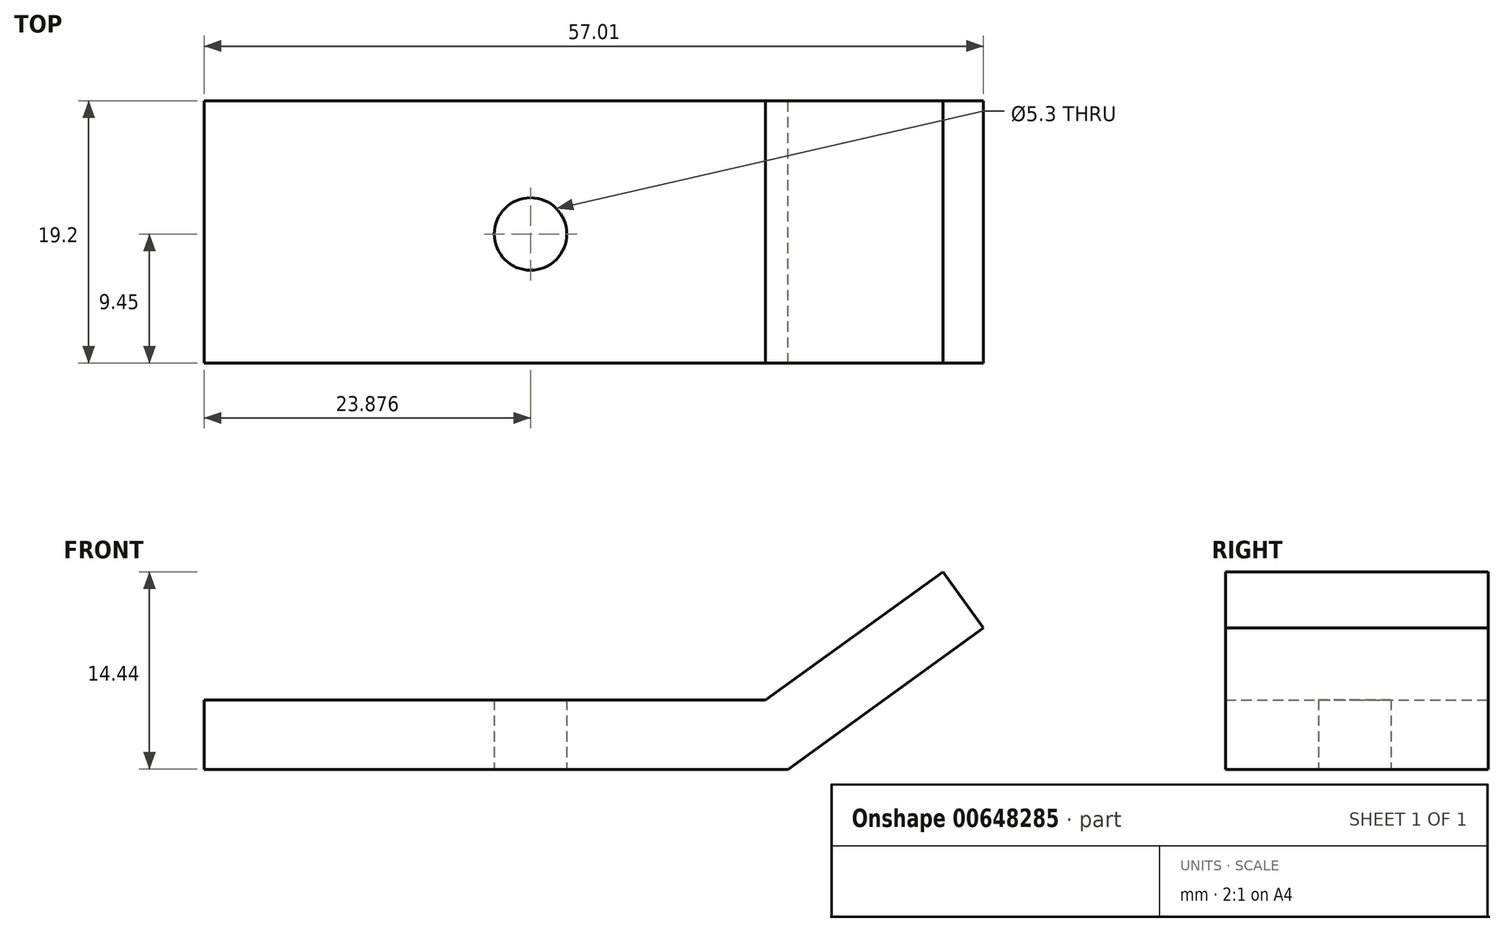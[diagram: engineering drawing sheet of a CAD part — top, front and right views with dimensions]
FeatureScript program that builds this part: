
annotation { "Feature Type Name" : "Feature", "Feature Type Description" : "" }
export const myFeature = defineFeature(function(context is Context, id is Id, definition is map)
    precondition{}
    {
        {
            var Q0;
            Q0=qCreatedBy(makeId("Front.planeOp"),FACE);
            var sketch = newSketch(context, id + "F0", { "sketchPlane" : qUnion([Q0])});
            skLineSegment(sketch, "E0", {"start": v(-38.7, -7.25) * mm, "end": v(4, -7.25) * mm});
            skLineSegment(sketch, "E1", {"start": v(4, -7.25) * mm, "end": v(18.3, 3.07) * mm});
            skLineSegment(sketch, "E2.0", {"start": v(2.36, -2.17) * mm, "end": v(15.33, 7.19) * mm});
            skLineSegment(sketch, "E3", {"start": v(2.36, -2.17) * mm, "end": v(-38.7, -2.17) * mm});
            skLineSegment(sketch, "E4", {"start": v(-38.7, -7.25) * mm, "end": v(-38.7, -2.17) * mm});
            skLineSegment(sketch, "E5", {"start": v(15.33, 7.19) * mm, "end": v(18.3, 3.07) * mm});
            skSolve(sketch);
        }
        {
            var Q0;
            Q0=makeQuery(id+"F0.imprint","IMPRINT",FACE,{"disambiguationData":[TD([[makeQuery(id+"F0.imprint","IMPRINT",EDGE,{"derivedFrom":sQuery(id+"F0.wireOp",EDGE,"E0")}),1.0]])]});
            var sketch = newSketch(context, id + "F1", { "sketchPlane" : qUnion([Q0])});
            skSolve(sketch);
        }
        {
            var Q0;
            Q0=makeQuery(id+"F0.imprint","IMPRINT",FACE,{"disambiguationData":[TD([[makeQuery(id+"F0.imprint","IMPRINT",EDGE,{"derivedFrom":sQuery(id+"F0.wireOp",EDGE,"E0")}),1.0]])]});
            extrude(context, id + "F2", {"entities" : qUnion([Q0]), "endBound" : BoundingType.SYMMETRIC, "depth" : 19.2 * mm, "offsetDistance" : 25.4 * mm});
        }
        {
            var Q0;
            Q0=makeQuery(id+"F1.imprint","IMPRINT",FACE,{"disambiguationData":[TD([[makeQuery(id+"F1.imprint","IMPRINT",EDGE,{"derivedFrom":makeQuery(id+"F0.imprint","IMPRINT",EDGE,{"derivedFrom":sQuery(id+"F0.wireOp",EDGE,"E0")})}),1.0]])]});
            var sketch = newSketch(context, id + "F3", { "sketchPlane" : qUnion([Q0])});
            skSolve(sketch);
        }
        {
            var Q0;
            Q0=makeQuery(id+"F2.opExtrude","SWEPT_FACE",FACE,{"disambiguationData":[OSD([sQuery(id+"F0.wireOp",EDGE,"E0")])]});
            var sketch = newSketch(context, id + "F4", { "sketchPlane" : qUnion([Q0])});
            skCircle(sketch, "E6", {"center": v(-14.82, 0.15) * mm, "radius": 2.65 * mm});
            skPoint(sketch, "E6.first.point", {"position": v(-17.47, 0) * mm});
            skPoint(sketch, "E6.second.point", {"position": v(-12.18, 0) * mm});
            skPoint(sketch, "E6.third.point", {"position": v(-17.35, 0.96) * mm});
            skPoint(sketch, "E6.third.point.positionSnap0", {"position": v(-17.35, -9.6) * mm});
            skSolve(sketch);
        }
        {
            var Q0;
            Q0 = qSketchRegion(id + "F4", true);
            extrude(context, id + "F5", {"entities" : qUnion([Q0]), "operationType" : NewBodyOperationType.REMOVE, "endBound" : BoundingType.THROUGH_ALL, "oppositeDirection" : true, "depth" : 25.4 * mm, "offsetDistance" : 25.4 * mm});
        }
    });
